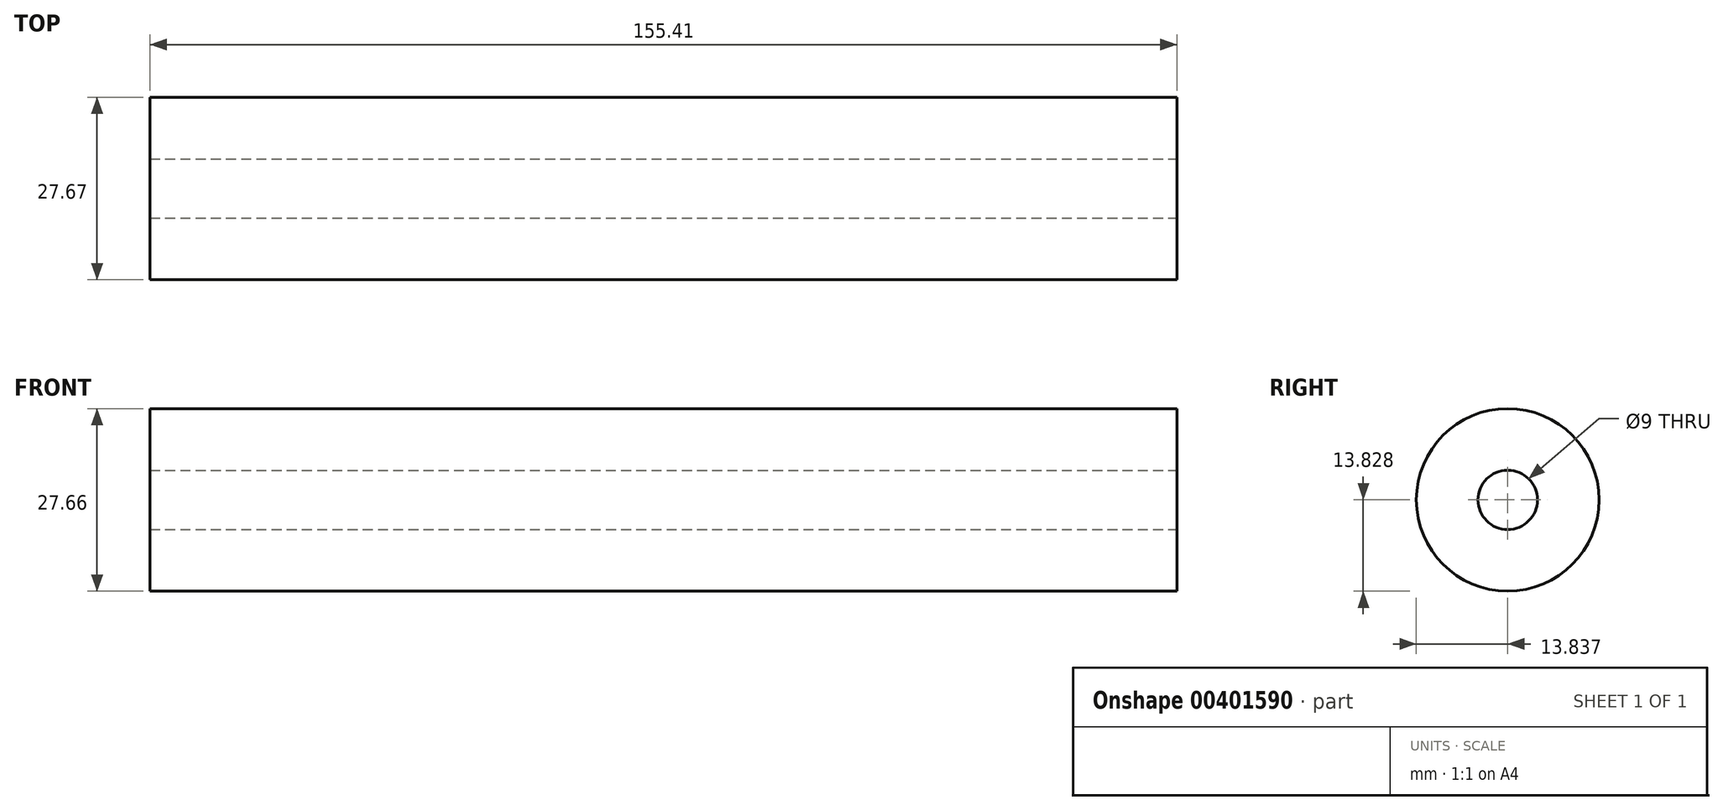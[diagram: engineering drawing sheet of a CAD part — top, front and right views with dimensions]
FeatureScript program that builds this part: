
annotation { "Feature Type Name" : "Feature", "Feature Type Description" : "" }
export const myFeature = defineFeature(function(context is Context, id is Id, definition is map)
    precondition{}
    {
        {
            var Q0;
            Q0=qCreatedBy(makeId("Right.planeOp"),FACE);
            var sketch = newSketch(context, id + "F0", { "sketchPlane" : qUnion([Q0])});
            skCircle(sketch, "E0", {"center": v(-32.8, 32.32) * mm, "radius": 13.83 * mm});
            skSolve(sketch);
        }
        {
            var Q0;
            Q0=makeQuery(id+"F0.imprint","IMPRINT",FACE,{"disambiguationData":[TD([[makeQuery(id+"F0.imprint","IMPRINT",EDGE,{"derivedFrom":sQuery(id+"F0.wireOp",EDGE,"E0")}),1.0]])]});
            var Q1;
            Q1=sQuery(id+"F0.wireOp",EDGE,"E0");
            extrude(context, id + "F1", {"entities" : qUnion([Q0]), "surfaceEntities" : qUnion([Q1]), "depth" : 155.4 * mm});
        }
        {
            var Q0;
            Q0=makeQuery(id+"F1.opExtrude","CAP_FACE",FACE,{"disambiguationData":[OSD([sQuery(id+"F0.wireOp",EDGE,"E0")])],"isStart":false});
            var sketch = newSketch(context, id + "F2", { "sketchPlane" : qUnion([Q0])});
            skPoint(sketch, "E1", {"position": v(-32.8, 32.32) * mm});
            skSolve(sketch);
        }
        {
            var Q0;
            Q0=sQuery(id+"F2.wireOp",VERTEX,"E1");
            var Q1;
            Q1=makeQuery(id+"F1.opExtrude","SWEPT_BODY",BODY,{"disambiguationData":[OSD([sQuery(id+"F0.wireOp",EDGE,"E0")])]});
            hole(context, id + "F3", {"style" : HoleStyle.SIMPLE, "endStyle" : HoleEndStyle.THROUGH, "holeDiameter" : 9 * mm, "isTappedThrough" : true, "tappedDepth" : 12 * mm, "tapClearance" : 3, "locations" : qUnion([Q0]), "scope" : qUnion([Q1])});
        }
    });
